# Revit family: Security_Camera-Dome-Vicon-Surface_Mount-Outdoor-CE202D_WN
name_source: partatom
category: Security Devices
revit_build: Autodesk Revit 2014 (Build: 20140709_2115(x64)
units: mm (PartAtom-declared; Revit-internal decimal feet)

## types (1)
- CE202D-WN
    Apparent Load = 5 VA
    Assembly Code = E1010110
    Connector Description = Connector for Electrical Power
    Connector Type = PoE/Network: RJ-45 CAT 5
    Default Elevation = 4' - 0"
    Description = Cost Effective Network Outdoor Camera Dome, Remotely Adjustable
    Housing Material = Plastic - Vicon - Beige
    Lens Material = Plastic - Vicon - Clear Acrylic
    Lens Option = CE202D FOV : 3.7mm
    Load Classification = Power
    Manufacturer = Vicon Industries
    Max Horizontal FOV = 89.00°
    Max Vertical FOV = 89.00°
    Max. Frame Rate = 30 fps
    Max. Resolution = 1080 P
    Max. Tilt Angle = 90 Degrees
    Min Horizontal FOV = 89.00°
    Min Vertical FOV = 89.00°
    Model = CE202D-WN
    Number of Poles = 1
    Operating Humidity = 0% to 80% non-condensing
    Operating Temperature = 14 to 113 Degrees Fahrenheit
    Power Factor = 1
    Product Documentation Link = http://www.vicon-security.com
    Product Page URL = http://www.vicon-security.com
    URL = http://www.vicon-security.com
    Voltage = 100 V
    Voltage Range = 12VDC, PoE
    Watts = 5 W
    Weight = 1.04 lb

## geometry (parser evidence)
native form markers: Blend x4, Sweep x3
no freeform markers — native parametric forms only
